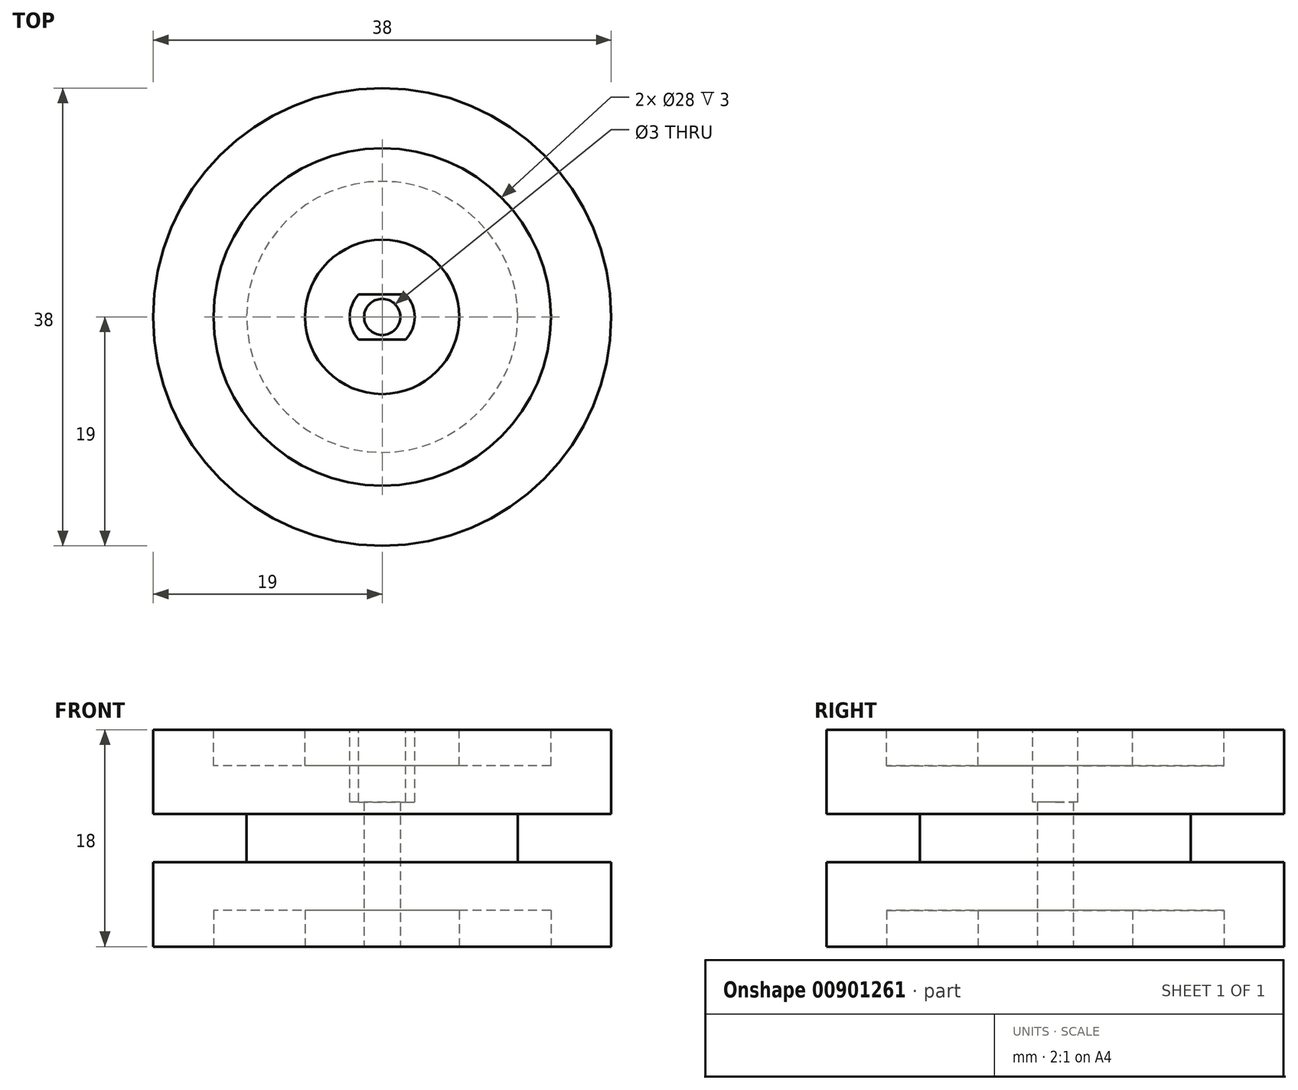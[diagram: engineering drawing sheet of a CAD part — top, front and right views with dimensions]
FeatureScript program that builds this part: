
annotation { "Feature Type Name" : "Feature", "Feature Type Description" : "" }
export const myFeature = defineFeature(function(context is Context, id is Id, definition is map)
    precondition{}
    {
        {
            var Q0;
            Q0=qCreatedBy(makeId("Top.planeOp"),FACE);
            var sketch = newSketch(context, id + "F0", { "sketchPlane" : qUnion([Q0])});
            skCircle(sketch, "E0", {"center": v(0, 0) * mm, "radius": 19 * mm});
            skSolve(sketch);
        }
        {
            var Q0;
            Q0=makeQuery(id+"F0.imprint","IMPRINT",FACE,{"disambiguationData":[TD([[makeQuery(id+"F0.imprint","IMPRINT",EDGE,{"derivedFrom":sQuery(id+"F0.wireOp",EDGE,"E0")}),1.0]])]});
            var Q1;
            Q1=makeQuery(id+"F0.imprint","IMPRINT",FACE,{"disambiguationData":[TD([[makeQuery(id+"F0.imprint","IMPRINT",EDGE,{"derivedFrom":sQuery(id+"F0.wireOp",EDGE,"Kd4oP0SL-7RFL-OBj8-Bmld-SwuPkdznoUvC")}),1.0]])]});
            extrude(context, id + "F1", {"entities" : qUnion([Q0, Q1]), "depth" : 7 * mm, "offsetDistance" : 25.4 * mm});
        }
        {
            var Q0;
            Q0=makeQuery(id+"F1.opExtrude","CAP_FACE",FACE,{"disambiguationData":[OSD([sQuery(id+"F0.wireOp",EDGE,"E0")])],"isStart":true});
            var sketch = newSketch(context, id + "F2", { "sketchPlane" : qUnion([Q0])});
            skCircle(sketch, "E1", {"center": v(0, 0) * mm, "radius": 11.25 * mm});
            skSolve(sketch);
        }
        {
            var Q0;
            Q0=makeQuery(id+"F2.imprint","IMPRINT",FACE,{"disambiguationData":[TD([[makeQuery(id+"F2.imprint","IMPRINT",EDGE,{"derivedFrom":sQuery(id+"F2.wireOp",EDGE,"E1")}),1.0]])]});
            extrude(context, id + "F3", {"entities" : qUnion([Q0]), "operationType" : NewBodyOperationType.ADD, "depth" : 2 * mm, "offsetDistance" : 25.4 * mm});
        }
        {
            var Q0;
            Q0=makeQuery(id+"F1.opExtrude","CAP_FACE",FACE,{"disambiguationData":[OSD([sQuery(id+"F0.wireOp",EDGE,"E0")])],"isStart":false});
            var sketch = newSketch(context, id + "F4", { "sketchPlane" : qUnion([Q0])});
            skCircle(sketch, "E2", {"center": v(0, 0) * mm, "radius": 14 * mm});
            skCircle(sketch, "E3", {"center": v(0, 0) * mm, "radius": 6.4 * mm});
            skSolve(sketch);
        }
        {
            var Q0;
            Q0=makeQuery(id+"F4.imprint","IMPRINT",FACE,{"disambiguationData":[TD([[makeQuery(id+"F4.imprint","IMPRINT",EDGE,{"derivedFrom":sQuery(id+"F4.wireOp",EDGE,"E2")}),1.0]])]});
            extrude(context, id + "F5", {"entities" : qUnion([Q0]), "operationType" : NewBodyOperationType.REMOVE, "oppositeDirection" : true, "depth" : 3 * mm, "offsetDistance" : 25.4 * mm});
        }
        {
            var Q0;
            Q0=makeQuery(id+"F1.opExtrude","SWEPT_BODY",BODY,{"disambiguationData":[OSD([sQuery(id+"F0.wireOp",EDGE,"E0")])]});
            var Q1;
            Q1=makeQuery(id+"F3.opExtrude","CAP_FACE",FACE,{"disambiguationData":[OSD([sQuery(id+"F2.wireOp",EDGE,"E1")])],"isStart":false});
            mirror(context, id + "F6", {"operationType" : NewBodyOperationType.ADD, "entities" : qUnion([Q0]), "mirrorPlane" : qUnion([Q1])});
        }
        {
            var Q0;
            Q0=makeQuery(id+"F5.boolean.opBoolean","SPLIT",FACE,{"disambiguationData":[TD([makeQuery(id+"F5.opExtrude","SWEPT_FACE",FACE,{"disambiguationData":[OSD([sQuery(id+"F4.wireOp",EDGE,"E3")])]})])],"derivedFrom":makeQuery(id+"F1.opExtrude","CAP_FACE",FACE,{"disambiguationData":[OSD([sQuery(id+"F0.wireOp",EDGE,"E0")])],"isStart":false})});
            var sketch = newSketch(context, id + "F7", { "sketchPlane" : qUnion([Q0])});
            skArc(sketch, "E4", {"start": v(-1.94, 1.87) * mm, "mid": v(-2.7, 0) * mm, "end": v(-1.94, -1.87) * mm});
            skLineSegment(sketch, "E5", {"start": v(-1.94, 1.87) * mm, "end": v(1.94, 1.88) * mm});
            skLineSegment(sketch, "E6", {"start": v(-1.94, -1.87) * mm, "end": v(1.94, -1.87) * mm});
            skArc(sketch, "E7.trimOffspring", {"start": v(1.94, -1.87) * mm, "mid": v(2.7, 0) * mm, "end": v(1.94, 1.87) * mm});
            skSolve(sketch);
        }
        {
            var Q0;
            Q0=makeQuery(id+"F7.imprint","IMPRINT",FACE,{"disambiguationData":[TD([[makeQuery(id+"F7.imprint","IMPRINT",EDGE,{"derivedFrom":sQuery(id+"F7.wireOp",EDGE,"E4")}),1.0]])]});
            extrude(context, id + "F8", {"entities" : qUnion([Q0]), "operationType" : NewBodyOperationType.REMOVE, "oppositeDirection" : true, "depth" : 6 * mm, "offsetDistance" : 25.4 * mm});
        }
        {
            var Q0;
            Q0=makeQuery(id+"F6.opPattern","COPY",FACE,{"derivedFrom":makeQuery(id+"F5.boolean.opBoolean","SPLIT",FACE,{"disambiguationData":[TD([makeQuery(id+"F5.opExtrude","SWEPT_FACE",FACE,{"disambiguationData":[OSD([sQuery(id+"F4.wireOp",EDGE,"E3")])]})])],"derivedFrom":makeQuery(id+"F1.opExtrude","CAP_FACE",FACE,{"disambiguationData":[OSD([sQuery(id+"F0.wireOp",EDGE,"E0")])],"isStart":false})}),"instanceName":"1"});
            var sketch = newSketch(context, id + "F9", { "sketchPlane" : qUnion([Q0])});
            skCircle(sketch, "E8", {"center": v(0, 0) * mm, "radius": 1.5 * mm});
            skSolve(sketch);
        }
        {
            var Q0;
            Q0=makeQuery(id+"F9.imprint","IMPRINT",FACE,{"disambiguationData":[TD([[makeQuery(id+"F9.imprint","IMPRINT",EDGE,{"derivedFrom":sQuery(id+"F9.wireOp",EDGE,"E8")}),1.0]])]});
            extrude(context, id + "F10", {"entities" : qUnion([Q0]), "operationType" : NewBodyOperationType.REMOVE, "endBound" : BoundingType.UP_TO_NEXT, "oppositeDirection" : true, "depth" : 25.4 * mm, "offsetDistance" : 25.4 * mm});
        }
    });
